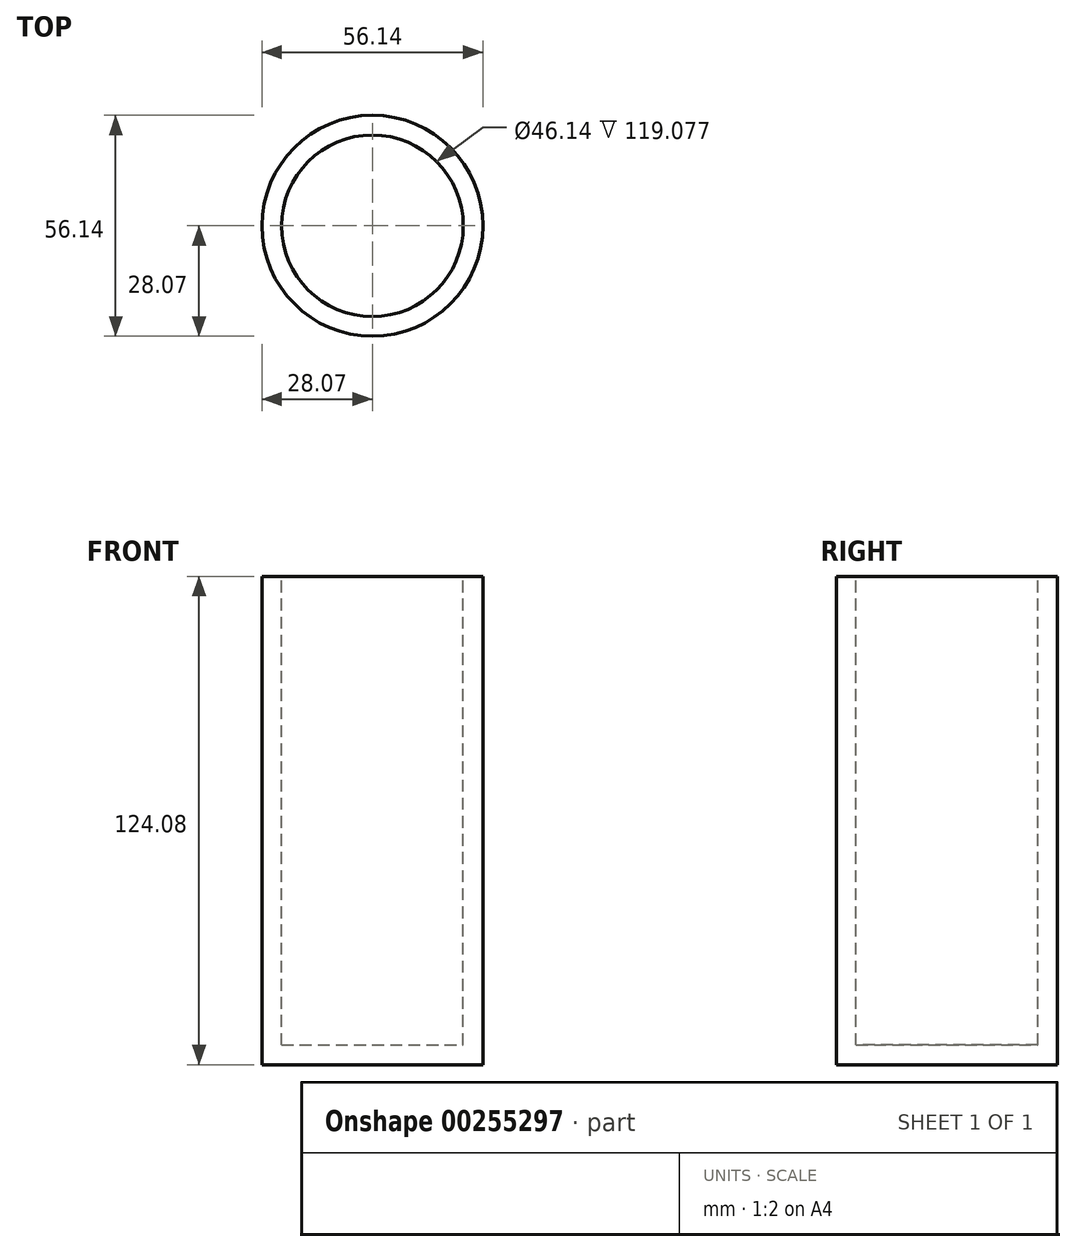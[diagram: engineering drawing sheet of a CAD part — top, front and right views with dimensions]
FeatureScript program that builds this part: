
annotation { "Feature Type Name" : "Feature", "Feature Type Description" : "" }
export const myFeature = defineFeature(function(context is Context, id is Id, definition is map)
    precondition{}
    {
        {
            var Q0;
            Q0=qCreatedBy(makeId("Front.planeOp"),FACE);
            var sketch = newSketch(context, id + "F0", { "sketchPlane" : qUnion([Q0])});
            skLineSegment(sketch, "E0.bottom", {"start": v(-28.07, 61.36) * mm, "end": v(34.27, 61.36) * mm});
            skLineSegment(sketch, "E0.top", {"start": v(-28.07, -62.72) * mm, "end": v(34.27, -62.72) * mm});
            skLineSegment(sketch, "E0.left", {"start": v(-28.07, 61.36) * mm, "end": v(-28.07, -62.72) * mm});
            skLineSegment(sketch, "E0.right", {"start": v(34.27, 61.36) * mm, "end": v(34.27, -62.72) * mm});
            skLineSegment(sketch, "E1", {"start": v(0, 0) * mm, "end": v(0, 63.73) * mm});
            skLineSegment(sketch, "E2", {"start": v(0, 0) * mm, "end": v(0, -62.72) * mm});
            skSolve(sketch);
        }
        {
            var Q0;
            {var subQ4=sQuery(id+"F0.wireOp",EDGE,"E0.left");Q0=makeQuery(id+"F0.imprint","IMPRINT",FACE,{"disambiguationData":[TD([[makeQuery(id+"F0.imprint","IMPRINT",EDGE,{"derivedFrom":subQ4}),1.0]])]});}
            var Q1;
            Q1=sQuery(id+"F0.wireOp",EDGE,"E2");
            revolve(context, id + "F1", {"entities" : qUnion([Q0]), "axis" : qUnion([Q1]), "revolveType" : RevolveType.FULL});
        }
        {
            var Q0;
            Q0=makeQuery(id+"F1.opRevolve","SWEPT_FACE",FACE,{"disambiguationData":[OSD([sQuery(id+"F0.wireOp",EDGE,"E0.bottom")])]});
            shell(context, id + "F2", {"entities" : qUnion([Q0]), "thickness" : 5 * mm});
        }
    });
